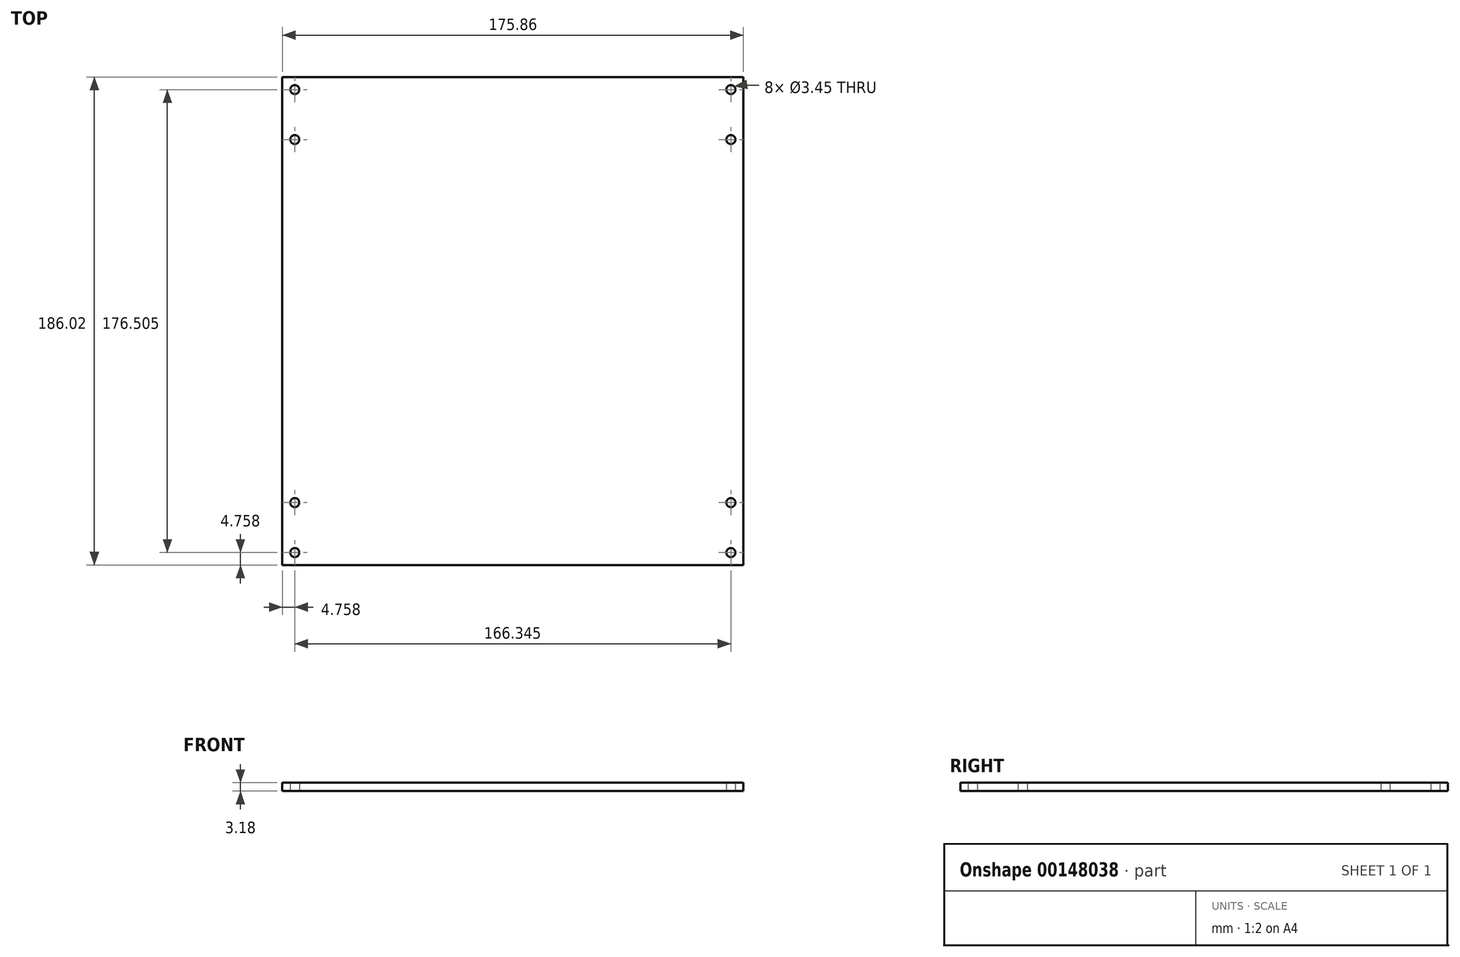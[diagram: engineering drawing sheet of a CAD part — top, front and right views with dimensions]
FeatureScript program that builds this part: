
annotation { "Feature Type Name" : "Feature", "Feature Type Description" : "" }
export const myFeature = defineFeature(function(context is Context, id is Id, definition is map)
    precondition{}
    {
        {
            var Q0;
            Q0=qCreatedBy(makeId("Top.planeOp"),FACE);
            var sketch = newSketch(context, id + "F0", { "sketchPlane" : qUnion([Q0])});
            skPoint(sketch, "E0.middle", {"position": v(0, 0) * mm});
            skLineSegment(sketch, "E1", {"start": v(0, 0) * mm, "end": v(0, 0) * mm});
            skLineSegment(sketch, "E2.bottom", {"start": v(-87.93, 93.01) * mm, "end": v(87.93, 93.01) * mm});
            skLineSegment(sketch, "E2.top", {"start": v(-87.93, -93.01) * mm, "end": v(87.93, -93.01) * mm});
            skLineSegment(sketch, "E2.left", {"start": v(-87.93, 93.01) * mm, "end": v(-87.93, -93.01) * mm});
            skLineSegment(sketch, "E2.right", {"start": v(87.93, 93.01) * mm, "end": v(87.93, -93.01) * mm});
            skLineSegment(sketch, "E3", {"start": v(-87.93, 88.25) * mm, "end": v(-83.17, 88.25) * mm, "construction": true});
            skLineSegment(sketch, "E4", {"start": v(-83.17, 88.25) * mm, "end": v(-83.17, 93.01) * mm, "construction": true});
            skLineSegment(sketch, "E5", {"start": v(-83.17, -93.01) * mm, "end": v(-83.17, -88.25) * mm, "construction": true});
            skLineSegment(sketch, "E6", {"start": v(-83.17, -88.25) * mm, "end": v(-83.17, -69.2) * mm, "construction": true});
            skLineSegment(sketch, "E7", {"start": v(83.17, 93.01) * mm, "end": v(83.17, 88.25) * mm, "construction": true});
            skLineSegment(sketch, "E8", {"start": v(83.17, 88.25) * mm, "end": v(87.93, 88.25) * mm, "construction": true});
            skLineSegment(sketch, "E9", {"start": v(83.17, 88.25) * mm, "end": v(83.17, 69.2) * mm, "construction": true});
            skLineSegment(sketch, "E10", {"start": v(-83.17, 88.25) * mm, "end": v(-83.17, 69.2) * mm, "construction": true});
            skLineSegment(sketch, "E11", {"start": v(83.17, -93.01) * mm, "end": v(83.17, -88.25) * mm, "construction": true});
            skLineSegment(sketch, "E12", {"start": v(83.17, -88.25) * mm, "end": v(83.17, -69.2) * mm, "construction": true});
            skCircle(sketch, "E13", {"center": v(-83.17, 88.25) * mm, "radius": 1.73 * mm});
            skCircle(sketch, "E14", {"center": v(-83.17, 69.2) * mm, "radius": 1.73 * mm});
            skCircle(sketch, "E15", {"center": v(-83.17, -69.2) * mm, "radius": 1.73 * mm});
            skCircle(sketch, "E16", {"center": v(-83.17, -88.25) * mm, "radius": 1.73 * mm});
            skCircle(sketch, "E17", {"center": v(83.17, -88.25) * mm, "radius": 1.73 * mm});
            skCircle(sketch, "E18", {"center": v(83.17, -69.2) * mm, "radius": 1.73 * mm});
            skCircle(sketch, "E19", {"center": v(83.17, 69.2) * mm, "radius": 1.73 * mm});
            skCircle(sketch, "E20", {"center": v(83.17, 88.25) * mm, "radius": 1.73 * mm});
            skSolve(sketch);
        }
        {
            var Q0;
            Q0=qSketchRegion(id+"F0",true);
            extrude(context, id + "F1", {"entities" : qUnion([Q0]), "depth" : 3.17 * mm});
        }
    });
